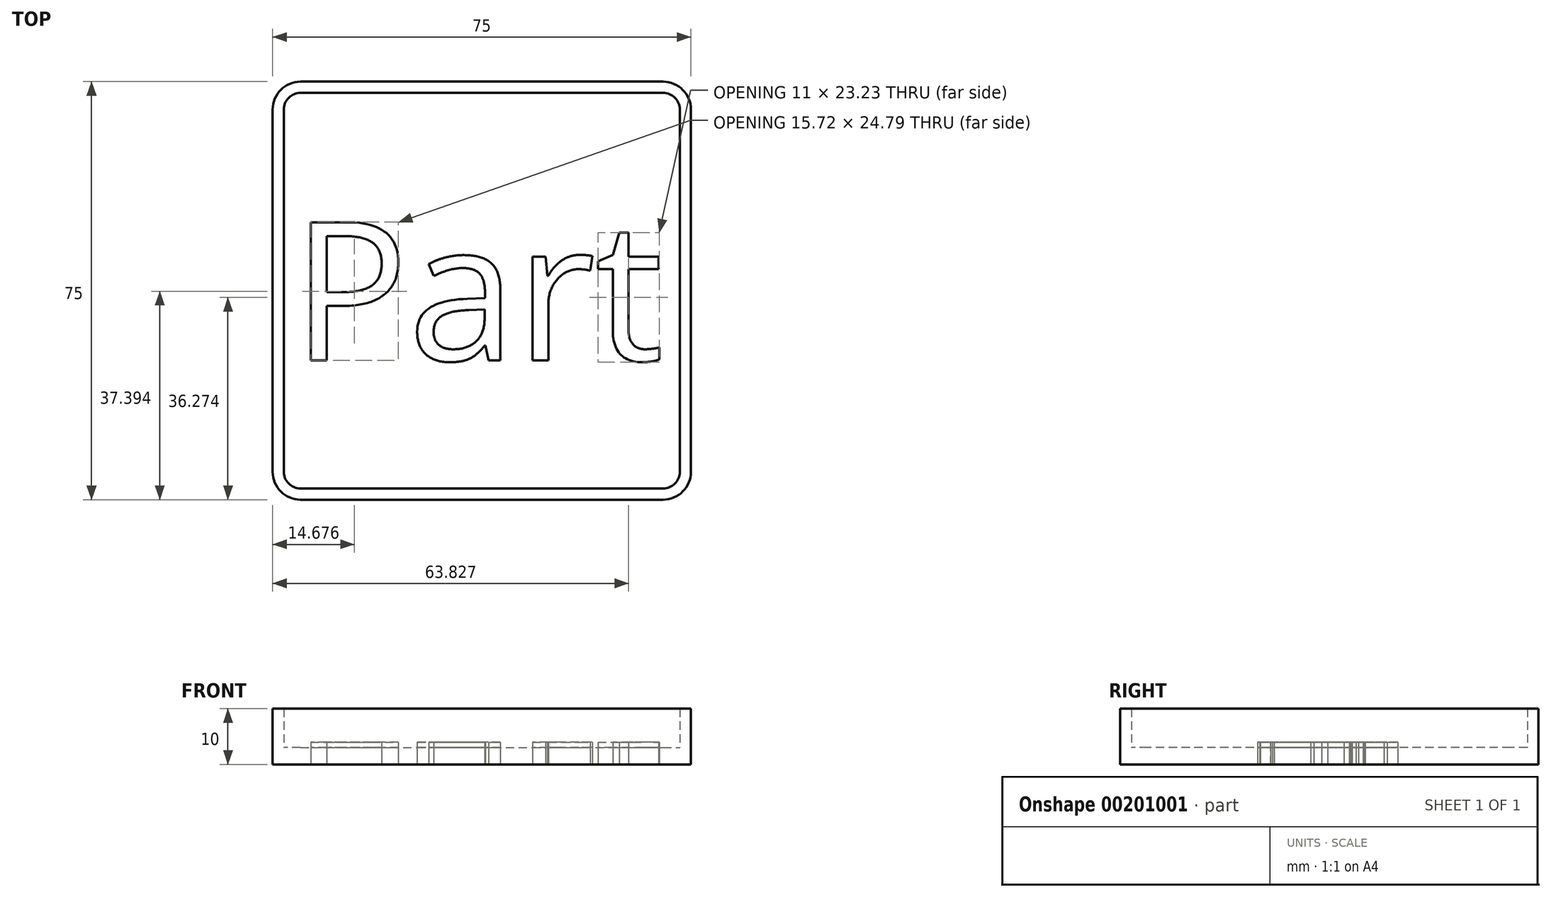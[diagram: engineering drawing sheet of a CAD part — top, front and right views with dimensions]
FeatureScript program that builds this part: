
annotation { "Feature Type Name" : "Feature", "Feature Type Description" : "" }
export const myFeature = defineFeature(function(context is Context, id is Id, definition is map)
    precondition{}
    {
        {
            var Q0;
            Q0=qCreatedBy(makeId("Top.planeOp"),FACE);
            var sketch = newSketch(context, id + "F0", { "sketchPlane" : qUnion([Q0])});
            skLineSegment(sketch, "E0.bottom", {"start": v(-41.61, 75) * mm, "end": v(23.39, 75) * mm});
            skLineSegment(sketch, "E0.top", {"start": v(-41.61, 0) * mm, "end": v(23.39, 0) * mm});
            skLineSegment(sketch, "E0.left", {"start": v(-46.61, 70) * mm, "end": v(-46.61, 5) * mm});
            skLineSegment(sketch, "E0.right", {"start": v(28.39, 70) * mm, "end": v(28.39, 5) * mm});
            skLineSegment(sketch, "E1.0", {"start": v(-41.61, 2) * mm, "end": v(23.39, 2) * mm});
            skLineSegment(sketch, "E1.1", {"start": v(-44.61, 70) * mm, "end": v(-44.61, 5) * mm});
            skLineSegment(sketch, "E1.2", {"start": v(-41.61, 73) * mm, "end": v(23.39, 73) * mm});
            skLineSegment(sketch, "E1.3", {"start": v(26.39, 70) * mm, "end": v(26.39, 5) * mm});
            skLineSegment(sketch, "E2", {"start": v(-9.11, 73) * mm, "end": v(-9.11, 2) * mm, "construction": true});
            skText(sketch, "E3", { "text": "Part", "fontName": "OpenSans-Regular.ttf"});
            skLineSegment(sketch, "E4", {"start": v(24.97, 37.5) * mm, "end": v(-43.2, 37.5) * mm, "construction": true});
            skLineSegment(sketch, "E5", {"start": v(-9.11, 37.5) * mm, "end": v(26.39, 37.5) * mm, "construction": true});
            skPoint(sketch, "E6.visualSharp", {"position": v(26.39, 73) * mm});
            skArc(sketch, "E6.filletArc", {"start": v(26.39, 70) * mm, "mid": v(25.5, 72.12) * mm, "end": v(23.39, 73) * mm});
            skPoint(sketch, "E7.visualSharp", {"position": v(-44.61, 73) * mm});
            skArc(sketch, "E7.filletArc", {"start": v(-41.61, 73) * mm, "mid": v(-43.73, 72.12) * mm, "end": v(-44.61, 70) * mm});
            skPoint(sketch, "E8.visualSharp", {"position": v(-44.61, 2) * mm});
            skArc(sketch, "E8.filletArc", {"start": v(-44.61, 5) * mm, "mid": v(-43.73, 2.88) * mm, "end": v(-41.61, 2) * mm});
            skPoint(sketch, "E9.visualSharp", {"position": v(26.39, 2) * mm});
            skArc(sketch, "E9.filletArc", {"start": v(23.39, 2) * mm, "mid": v(25.5, 2.88) * mm, "end": v(26.39, 5) * mm});
            skPoint(sketch, "E10.visualSharp", {"position": v(28.39, 0) * mm});
            skArc(sketch, "E10.filletArc", {"start": v(23.39, 0) * mm, "mid": v(26.92, 1.46) * mm, "end": v(28.39, 5) * mm});
            skPoint(sketch, "E11.visualSharp", {"position": v(28.39, 75) * mm});
            skArc(sketch, "E11.filletArc", {"start": v(28.39, 70) * mm, "mid": v(26.92, 73.54) * mm, "end": v(23.39, 75) * mm});
            skPoint(sketch, "E12.visualSharp", {"position": v(-46.61, 75) * mm});
            skArc(sketch, "E12.filletArc", {"start": v(-41.61, 75) * mm, "mid": v(-45.15, 73.54) * mm, "end": v(-46.61, 70) * mm});
            skPoint(sketch, "E13.visualSharp", {"position": v(-46.61, 0) * mm});
            skArc(sketch, "E13.filletArc", {"start": v(-46.61, 5) * mm, "mid": v(-45.15, 1.46) * mm, "end": v(-41.61, 0) * mm});
            const initialGuessF0  = {"E3": [-0.0432, 0.025, 1, 0, 0.025]};
            skSetInitialGuess(sketch, initialGuessF0);
            skSolve(sketch);
        }
        {
            var Q0;
            Q0=makeQuery(id+"F0.imprint","IMPRINT",FACE,{"disambiguationData":[TD([[makeQuery(id+"F0.imprint","IMPRINT",EDGE,{"derivedFrom":sQuery(id+"F0.wireOp",EDGE,"E1.0")}),1.0]])]});
            var Q1;
            Q1=makeQuery(id+"F0.imprint","IMPRINT",FACE,{"disambiguationData":[TD([[makeQuery(id+"F0.imprint","IMPRINT",EDGE,{"derivedFrom":sQuery(id+"F0.wireOp",EDGE,"E3.sketch_text.stroke-63")}),1.0]])]});
            var Q2;
            Q2=makeQuery(id+"F0.imprint","IMPRINT",FACE,{"disambiguationData":[TD([[makeQuery(id+"F0.imprint","IMPRINT",EDGE,{"derivedFrom":sQuery(id+"F0.wireOp",EDGE,"E3.sketch_text.stroke-17")}),1.0]])]});
            var Q3;
            Q3=makeQuery(id+"F0.imprint","IMPRINT",FACE,{"disambiguationData":[TD([[makeQuery(id+"F0.imprint","IMPRINT",EDGE,{"derivedFrom":sQuery(id+"F0.wireOp",EDGE,"E3.sketch_text.stroke-34")}),1.0]])]});
            var Q4;
            Q4=makeQuery(id+"F0.imprint","IMPRINT",FACE,{"disambiguationData":[TD([[makeQuery(id+"F0.imprint","IMPRINT",EDGE,{"derivedFrom":sQuery(id+"F0.wireOp",EDGE,"E3.sketch_text.stroke-8")}),1.0]])]});
            extrude(context, id + "F1", {"entities" : qUnion([Q0, Q1, Q2, Q3, Q4]), "depth" : 3 * mm});
        }
        {
            var Q0;
            Q0=makeQuery(id+"F0.imprint","IMPRINT",FACE,{"disambiguationData":[TD([[makeQuery(id+"F0.imprint","IMPRINT",EDGE,{"derivedFrom":sQuery(id+"F0.wireOp",EDGE,"E0.bottom")}),-1.0]])]});
            extrude(context, id + "F2", {"entities" : qUnion([Q0]), "operationType" : NewBodyOperationType.ADD, "depth" : 10 * mm});
        }
        {
            var Q0;
            Q0=makeQuery(id+"F0.imprint","IMPRINT",FACE,{"disambiguationData":[TD([[makeQuery(id+"F0.imprint","IMPRINT",EDGE,{"derivedFrom":sQuery(id+"F0.wireOp",EDGE,"E3.sketch_text.stroke-0")}),-1.0]])]});
            var Q1;
            Q1=makeQuery(id+"F0.imprint","IMPRINT",FACE,{"disambiguationData":[TD([[makeQuery(id+"F0.imprint","IMPRINT",EDGE,{"derivedFrom":sQuery(id+"F0.wireOp",EDGE,"E3.sketch_text.stroke-8")}),-1.0]])]});
            var Q2;
            Q2=makeQuery(id+"F0.imprint","IMPRINT",FACE,{"disambiguationData":[TD([[makeQuery(id+"F0.imprint","IMPRINT",EDGE,{"derivedFrom":sQuery(id+"F0.wireOp",EDGE,"E3.sketch_text.stroke-25")}),-1.0]])]});
            var Q3;
            Q3=makeQuery(id+"F0.imprint","IMPRINT",FACE,{"disambiguationData":[TD([[makeQuery(id+"F0.imprint","IMPRINT",EDGE,{"derivedFrom":sQuery(id+"F0.wireOp",EDGE,"E3.sketch_text.stroke-44")}),-1.0]])]});
            var Q4;
            Q4=makeQuery(id+"F0.imprint","IMPRINT",FACE,{"disambiguationData":[TD([[makeQuery(id+"F0.imprint","IMPRINT",EDGE,{"derivedFrom":sQuery(id+"F0.wireOp",EDGE,"E3.sketch_text.stroke-71")}),-1.0]])]});
            extrude(context, id + "F3", {"entities" : qUnion([Q0, Q1, Q2, Q3, Q4]), "depth" : 4 * mm});
        }
    });
